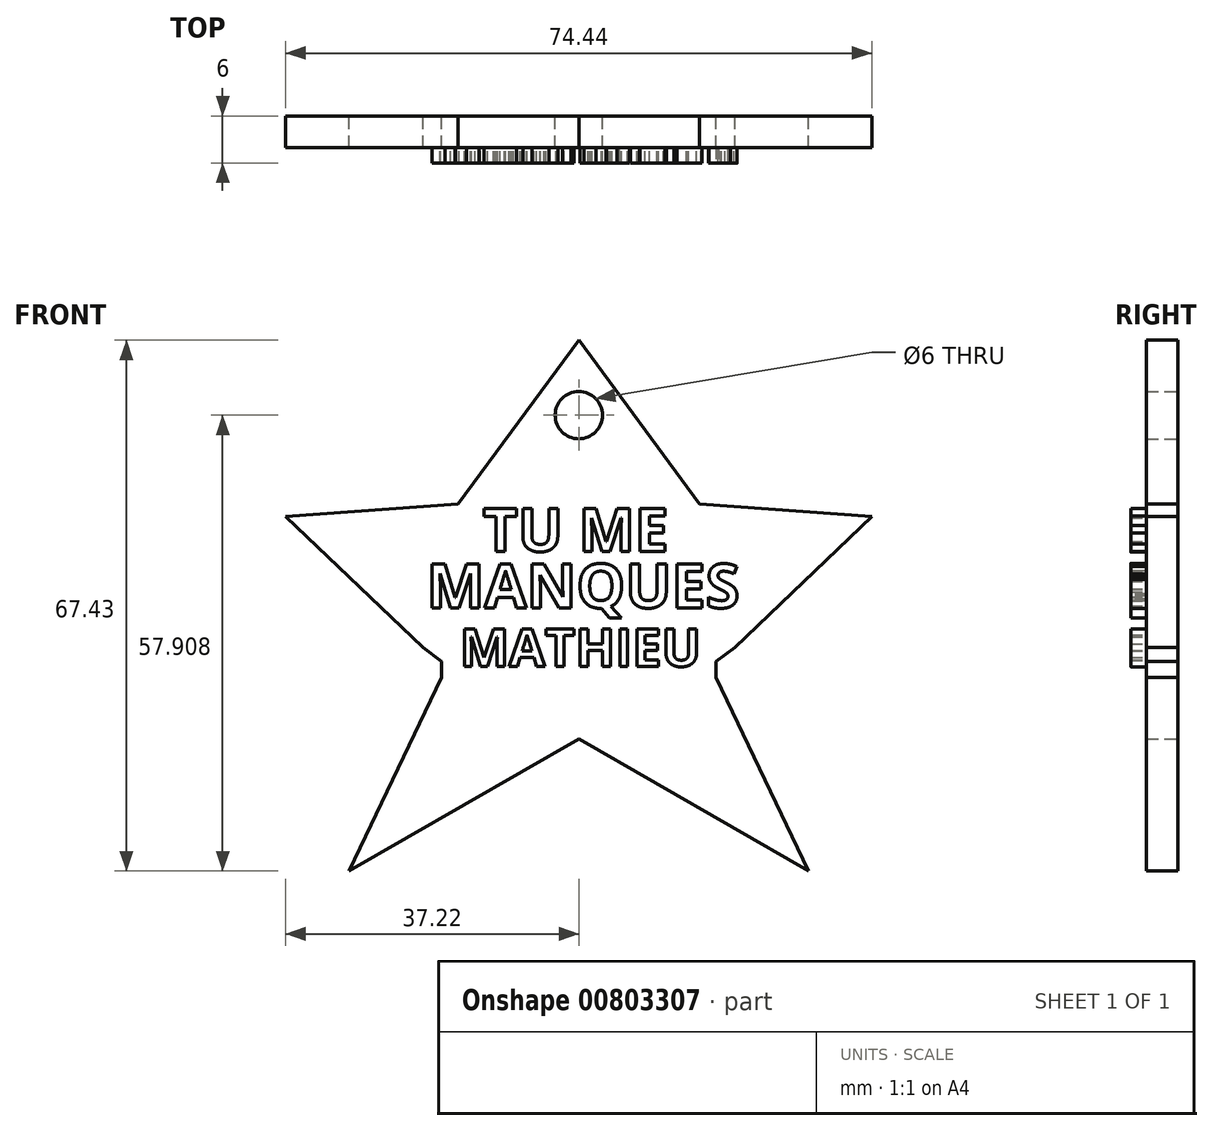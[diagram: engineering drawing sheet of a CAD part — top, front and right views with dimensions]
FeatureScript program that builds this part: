
annotation { "Feature Type Name" : "Feature", "Feature Type Description" : "" }
export const myFeature = defineFeature(function(context is Context, id is Id, definition is map)
    precondition{}
    {
        {
            var Q0;
            Q0=qCreatedBy(makeId("Front.planeOp"),FACE);
            var sketch = newSketch(context, id + "F0", { "sketchPlane" : qUnion([Q0])});
            skLineSegment(sketch, "E0", {"start": v(0, 54) * mm, "end": v(-15.3, 33.18) * mm});
            skLineSegment(sketch, "E1", {"start": v(-15.3, 33.18) * mm, "end": v(-37.22, 31.63) * mm});
            skLineSegment(sketch, "E2", {"start": v(-37.22, 31.63) * mm, "end": v(-19.82, 15) * mm});
            skLineSegment(sketch, "E3", {"start": v(-19.82, 15) * mm, "end": v(-17.41, 13.23) * mm});
            skLineSegment(sketch, "E4", {"start": v(-17.41, 11.17) * mm, "end": v(-29.2, -13.42) * mm});
            skLineSegment(sketch, "E5", {"start": v(-17.41, 11.17) * mm, "end": v(-17.41, 13.23) * mm});
            skLineSegment(sketch, "E6", {"start": v(-29.2, -13.42) * mm, "end": v(0, 3.35) * mm});
            skLineSegment(sketch, "E7", {"start": v(0, 3.35) * mm, "end": v(0, 3.35) * mm});
            skLineSegment(sketch, "E8.MirrorCS", {"start": v(0, 54) * mm, "end": v(15.3, 33.18) * mm});
            skLineSegment(sketch, "E9.MirrorCS", {"start": v(15.3, 33.18) * mm, "end": v(37.22, 31.63) * mm});
            skLineSegment(sketch, "E10.MirrorCS", {"start": v(37.22, 31.63) * mm, "end": v(19.82, 15) * mm});
            skLineSegment(sketch, "E11.MirrorCS", {"start": v(17.41, 11.17) * mm, "end": v(29.2, -13.42) * mm});
            skLineSegment(sketch, "E12.MirrorCS", {"start": v(29.2, -13.42) * mm, "end": v(0, 3.35) * mm});
            skLineSegment(sketch, "E13.MirrorCS", {"start": v(19.82, 15) * mm, "end": v(17.41, 13.23) * mm});
            skLineSegment(sketch, "E14.MirrorCS", {"start": v(17.41, 11.17) * mm, "end": v(17.41, 13.23) * mm});
            skText(sketch, "E15", { "text": "TU ME \n", "fontName": "OpenSans-Bold.ttf"});
            skText(sketch, "E16", { "text": "MANQUES", "fontName": "OpenSans-Bold.ttf"});
            skText(sketch, "E17", { "text": "MATHIEU", "fontName": "OpenSans-Bold.ttf"});
            skCircle(sketch, "E18", {"center": v(0, 44.49) * mm, "radius": 3 * mm});
            const initialGuessF0  = {"E15": [-0.01216, 0.02718, 1, 0, 0.00547], "E16": [-0.01932, 0.02002, 1, 0, 0.0056], "E17": [-0.01511, 0.01258, 1, 0, 0.00477]};
            skSetInitialGuess(sketch, initialGuessF0);
            skSolve(sketch);
        }
        {
            var Q0;
            Q0=makeQuery(id+"F0.imprint","IMPRINT",FACE,{"disambiguationData":[TD([[makeQuery(id+"F0.imprint","IMPRINT",EDGE,{"derivedFrom":sQuery(id+"F0.wireOp",EDGE,"E0")}),1.0]])]});
            var Q1;
            Q1=makeQuery(id+"F0.imprint","IMPRINT",FACE,{"disambiguationData":[TD([[makeQuery(id+"F0.imprint","IMPRINT",EDGE,{"derivedFrom":sQuery(id+"F0.wireOp",EDGE,"E16.sketch_text.stroke-57")}),1.0]])]});
            var Q2;
            Q2=makeQuery(id+"F0.imprint","IMPRINT",FACE,{"disambiguationData":[TD([[makeQuery(id+"F0.imprint","IMPRINT",EDGE,{"derivedFrom":sQuery(id+"F0.wireOp",EDGE,"E17.sketch_text.stroke-27")}),1.0]])]});
            var Q3;
            Q3=makeQuery(id+"F0.imprint","IMPRINT",FACE,{"disambiguationData":[TD([[makeQuery(id+"F0.imprint","IMPRINT",EDGE,{"derivedFrom":sQuery(id+"F0.wireOp",EDGE,"E16.sketch_text.stroke-27")}),1.0]])]});
            extrude(context, id + "F1", {"entities" : qUnion([Q0, Q1, Q2, Q3]), "depth" : 4 * mm, "offsetDistance" : 25 * mm});
        }
        {
            var Q0;
            Q0=makeQuery(id+"F0.imprint","IMPRINT",FACE,{"disambiguationData":[TD([[makeQuery(id+"F0.imprint","IMPRINT",EDGE,{"derivedFrom":sQuery(id+"F0.wireOp",EDGE,"E17.sketch_text.stroke-0")}),-1.0]])]});
            var Q1;
            Q1=makeQuery(id+"F0.imprint","IMPRINT",FACE,{"disambiguationData":[TD([[makeQuery(id+"F0.imprint","IMPRINT",EDGE,{"derivedFrom":sQuery(id+"F0.wireOp",EDGE,"E17.sketch_text.stroke-19")}),-1.0]])]});
            var Q2;
            Q2=makeQuery(id+"F0.imprint","IMPRINT",FACE,{"disambiguationData":[TD([[makeQuery(id+"F0.imprint","IMPRINT",EDGE,{"derivedFrom":sQuery(id+"F0.wireOp",EDGE,"E17.sketch_text.stroke-31")}),-1.0]])]});
            var Q3;
            Q3=makeQuery(id+"F0.imprint","IMPRINT",FACE,{"disambiguationData":[TD([[makeQuery(id+"F0.imprint","IMPRINT",EDGE,{"derivedFrom":sQuery(id+"F0.wireOp",EDGE,"E17.sketch_text.stroke-39")}),-1.0]])]});
            var Q4;
            Q4=makeQuery(id+"F0.imprint","IMPRINT",FACE,{"disambiguationData":[TD([[makeQuery(id+"F0.imprint","IMPRINT",EDGE,{"derivedFrom":sQuery(id+"F0.wireOp",EDGE,"E17.sketch_text.stroke-51")}),-1.0]])]});
            var Q5;
            Q5=makeQuery(id+"F0.imprint","IMPRINT",FACE,{"disambiguationData":[TD([[makeQuery(id+"F0.imprint","IMPRINT",EDGE,{"derivedFrom":sQuery(id+"F0.wireOp",EDGE,"E17.sketch_text.stroke-55")}),-1.0]])]});
            var Q6;
            Q6=makeQuery(id+"F0.imprint","IMPRINT",FACE,{"disambiguationData":[TD([[makeQuery(id+"F0.imprint","IMPRINT",EDGE,{"derivedFrom":sQuery(id+"F0.wireOp",EDGE,"E17.sketch_text.stroke-67")}),-1.0]])]});
            var Q7;
            Q7=makeQuery(id+"F0.imprint","IMPRINT",FACE,{"disambiguationData":[TD([[makeQuery(id+"F0.imprint","IMPRINT",EDGE,{"derivedFrom":sQuery(id+"F0.wireOp",EDGE,"E16.sketch_text.stroke-0")}),-1.0]])]});
            var Q8;
            Q8=makeQuery(id+"F0.imprint","IMPRINT",FACE,{"disambiguationData":[TD([[makeQuery(id+"F0.imprint","IMPRINT",EDGE,{"derivedFrom":sQuery(id+"F0.wireOp",EDGE,"E16.sketch_text.stroke-19")}),-1.0]])]});
            var Q9;
            Q9=makeQuery(id+"F0.imprint","IMPRINT",FACE,{"disambiguationData":[TD([[makeQuery(id+"F0.imprint","IMPRINT",EDGE,{"derivedFrom":sQuery(id+"F0.wireOp",EDGE,"E16.sketch_text.stroke-31")}),-1.0]])]});
            var Q10;
            Q10=makeQuery(id+"F0.imprint","IMPRINT",FACE,{"disambiguationData":[TD([[makeQuery(id+"F0.imprint","IMPRINT",EDGE,{"derivedFrom":sQuery(id+"F0.wireOp",EDGE,"E16.sketch_text.stroke-45")}),-1.0]])]});
            var Q11;
            Q11=makeQuery(id+"F0.imprint","IMPRINT",FACE,{"disambiguationData":[TD([[makeQuery(id+"F0.imprint","IMPRINT",EDGE,{"derivedFrom":sQuery(id+"F0.wireOp",EDGE,"E16.sketch_text.stroke-63")}),-1.0]])]});
            var Q12;
            Q12=makeQuery(id+"F0.imprint","IMPRINT",FACE,{"disambiguationData":[TD([[makeQuery(id+"F0.imprint","IMPRINT",EDGE,{"derivedFrom":sQuery(id+"F0.wireOp",EDGE,"E16.sketch_text.stroke-78")}),-1.0]])]});
            var Q13;
            Q13=makeQuery(id+"F0.imprint","IMPRINT",FACE,{"disambiguationData":[TD([[makeQuery(id+"F0.imprint","IMPRINT",EDGE,{"derivedFrom":sQuery(id+"F0.wireOp",EDGE,"E16.sketch_text.stroke-90")}),-1.0]])]});
            var Q14;
            Q14=makeQuery(id+"F0.imprint","IMPRINT",FACE,{"disambiguationData":[TD([[makeQuery(id+"F0.imprint","IMPRINT",EDGE,{"derivedFrom":sQuery(id+"F0.wireOp",EDGE,"E15.sketch_text.stroke-42")}),-1.0]])]});
            var Q15;
            Q15=makeQuery(id+"F0.imprint","IMPRINT",FACE,{"disambiguationData":[TD([[makeQuery(id+"F0.imprint","IMPRINT",EDGE,{"derivedFrom":sQuery(id+"F0.wireOp",EDGE,"E15.sketch_text.stroke-23")}),-1.0]])]});
            var Q16;
            Q16=makeQuery(id+"F0.imprint","IMPRINT",FACE,{"disambiguationData":[TD([[makeQuery(id+"F0.imprint","IMPRINT",EDGE,{"derivedFrom":sQuery(id+"F0.wireOp",EDGE,"E15.sketch_text.stroke-8")}),-1.0]])]});
            var Q17;
            Q17=makeQuery(id+"F0.imprint","IMPRINT",FACE,{"disambiguationData":[TD([[makeQuery(id+"F0.imprint","IMPRINT",EDGE,{"derivedFrom":sQuery(id+"F0.wireOp",EDGE,"E15.sketch_text.stroke-0")}),-1.0]])]});
            extrude(context, id + "F2", {"entities" : qUnion([Q0, Q1, Q2, Q3, Q4, Q5, Q6, Q7, Q8, Q9, Q10, Q11, Q12, Q13, Q14, Q15, Q16, Q17]), "operationType" : NewBodyOperationType.ADD, "depth" : 6 * mm, "offsetDistance" : 25 * mm});
        }
    });
